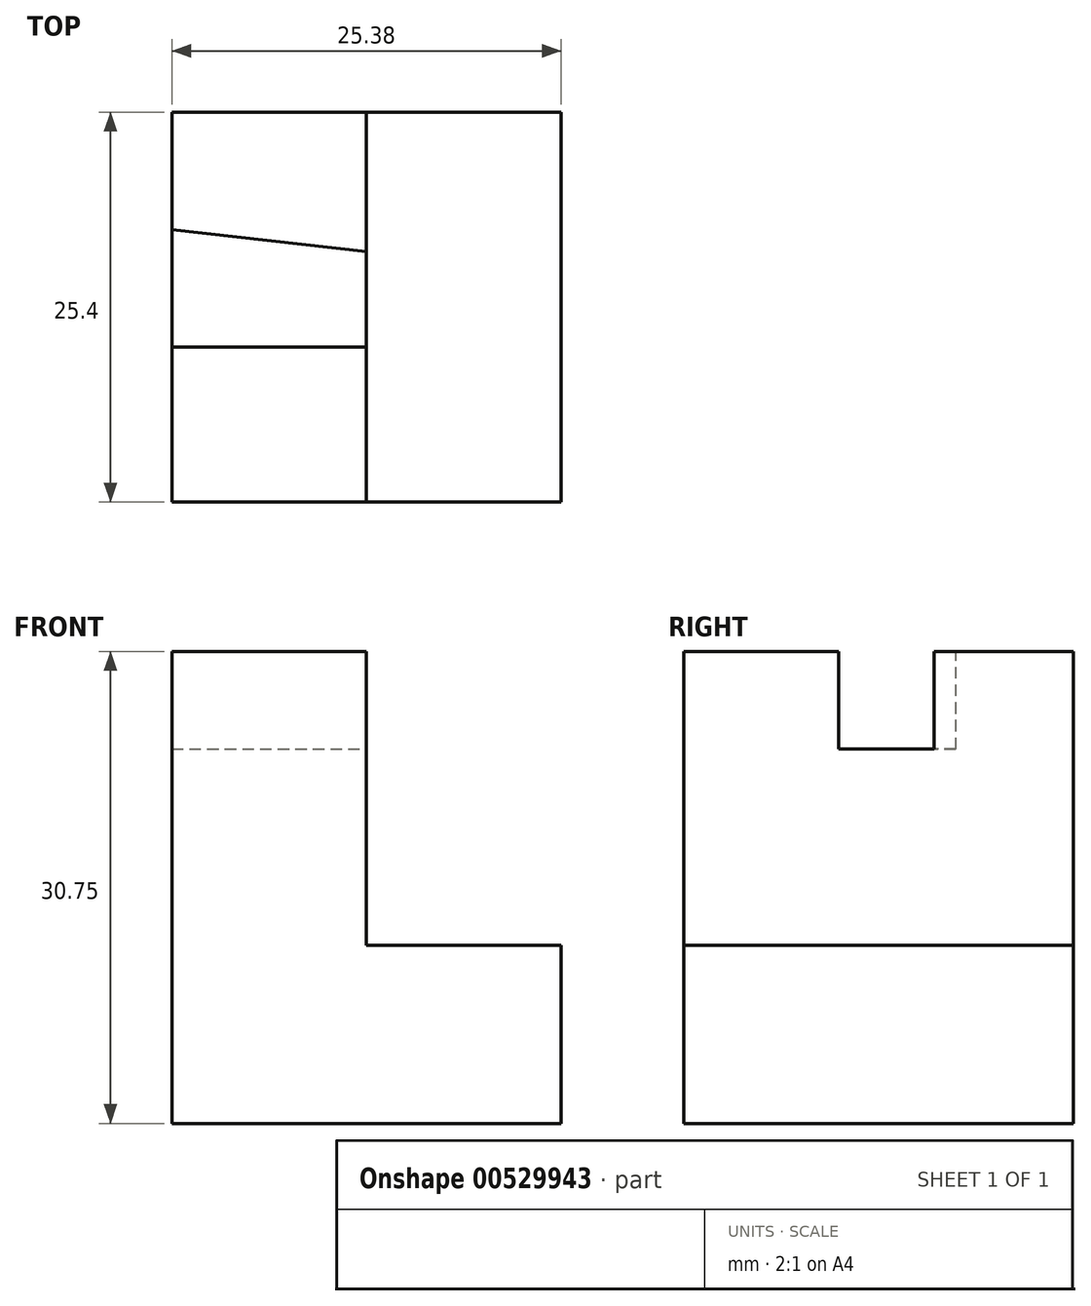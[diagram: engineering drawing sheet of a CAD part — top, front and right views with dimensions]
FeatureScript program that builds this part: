
annotation { "Feature Type Name" : "Feature", "Feature Type Description" : "" }
export const myFeature = defineFeature(function(context is Context, id is Id, definition is map)
    precondition{}
    {
        {
            var Q0;
            Q0=qCreatedBy(makeId("Front.planeOp"),FACE);
            var sketch = newSketch(context, id + "F0", { "sketchPlane" : qUnion([Q0])});
            skLineSegment(sketch, "E0.bottom", {"start": v(-57, 56.92) * mm, "end": v(-18.9, 56.92) * mm});
            skLineSegment(sketch, "E0.top", {"start": v(-57, 26.17) * mm, "end": v(-18.9, 26.17) * mm});
            skLineSegment(sketch, "E0.left", {"start": v(-57, 56.92) * mm, "end": v(-57, 26.17) * mm});
            skLineSegment(sketch, "E0.right", {"start": v(-18.9, 56.92) * mm, "end": v(-18.9, 26.17) * mm});
            skSolve(sketch);
        }
        {
            var Q0;
            Q0=makeQuery(id+"F0.imprint","IMPRINT",FACE,{"disambiguationData":[TD([[makeQuery(id+"F0.imprint","IMPRINT",EDGE,{"derivedFrom":sQuery(id+"F0.wireOp",EDGE,"E0.bottom")}),-1.0]])]});
            extrude(context, id + "F1", {"entities" : qUnion([Q0]), "depth" : 25.4 * mm, "offsetDistance" : 25.4 * mm});
        }
        {
            var Q0;
            Q0=makeQuery(id+"F1.opExtrude","SWEPT_FACE",FACE,{"disambiguationData":[OSD([sQuery(id+"F0.wireOp",EDGE,"E0.right")])]});
            var sketch = newSketch(context, id + "F2", { "sketchPlane" : qUnion([Q0])});
            skLineSegment(sketch, "E1", {"start": v(-25.4, 56.92) * mm, "end": v(-25.4, 37.78) * mm});
            skLineSegment(sketch, "E2", {"start": v(-25.4, 37.78) * mm, "end": v(0, 37.78) * mm});
            skLineSegment(sketch, "E3", {"start": v(0, 37.78) * mm, "end": v(0, 56.92) * mm});
            skLineSegment(sketch, "E4", {"start": v(0, 56.92) * mm, "end": v(-25.4, 56.92) * mm});
            skSolve(sketch);
        }
        {
            var Q0;
            Q0=makeQuery(id+"F2.imprint","IMPRINT",FACE,{"disambiguationData":[TD([[makeQuery(id+"F2.imprint","IMPRINT",EDGE,{"derivedFrom":sQuery(id+"F2.wireOp",EDGE,"E1")}),1.0]])]});
            extrude(context, id + "F3", {"entities" : qUnion([Q0]), "operationType" : NewBodyOperationType.REMOVE, "oppositeDirection" : true, "depth" : 12.7 * mm, "offsetDistance" : 25.4 * mm});
        }
        {
            var Q0;
            Q0=makeQuery(id+"F1.opExtrude","CAP_FACE",FACE,{"disambiguationData":[OSD([sQuery(id+"F0.wireOp",EDGE,"E0.bottom"),sQuery(id+"F0.wireOp",EDGE,"E0.top"),sQuery(id+"F0.wireOp",EDGE,"E0.left"),sQuery(id+"F0.wireOp",EDGE,"E0.right")])],"isStart":true});
            var sketch = newSketch(context, id + "F4", { "sketchPlane" : qUnion([Q0])});
            skLineSegment(sketch, "E5", {"start": v(18.9, 26.17) * mm, "end": v(44.28, 26.17) * mm});
            skLineSegment(sketch, "E6", {"start": v(44.28, 26.17) * mm, "end": v(44.28, 56.92) * mm});
            skSolve(sketch);
        }
        {
            var Q0;
            {var subQ0=sQuery(id+"F4.wireOp",EDGE,"E6");Q0=makeQuery(id+"F4.imprint","IMPRINT",FACE,{"disambiguationData":[TD([[makeQuery(id+"F4.imprint","IMPRINT",EDGE,{"derivedFrom":subQ0}),-1.0]])]});}
            extrude(context, id + "F5", {"entities" : qUnion([Q0]), "operationType" : NewBodyOperationType.REMOVE, "oppositeDirection" : true, "depth" : 25.4 * mm, "offsetDistance" : 25.4 * mm});
        }
        {
            var Q0;
            Q0=makeQuery(id+"F1.opExtrude","SWEPT_FACE",FACE,{"disambiguationData":[OSD([sQuery(id+"F0.wireOp",EDGE,"E0.bottom")])]});
            var sketch = newSketch(context, id + "F6", { "sketchPlane" : qUnion([Q0])});
            skLineSegment(sketch, "E7", {"start": v(-44.28, -25.4) * mm, "end": v(-44.28, -15.31) * mm});
            skLineSegment(sketch, "E8", {"start": v(-44.28, -15.31) * mm, "end": v(-31.6, -15.31) * mm});
            skLineSegment(sketch, "E9", {"start": v(-31.6, -15.31) * mm, "end": v(-31.6, -25.4) * mm});
            skLineSegment(sketch, "E10", {"start": v(-31.6, -25.4) * mm, "end": v(-44.28, -25.4) * mm});
            skLineSegment(sketch, "E11", {"start": v(-44.28, 0) * mm, "end": v(-44.28, -7.65) * mm});
            skLineSegment(sketch, "E12", {"start": v(-44.28, -7.65) * mm, "end": v(-31.6, -9.1) * mm});
            skLineSegment(sketch, "E13", {"start": v(-31.6, -9.1) * mm, "end": v(-31.6, 0) * mm});
            skLineSegment(sketch, "E14", {"start": v(-31.6, 0) * mm, "end": v(-44.28, 0) * mm});
            skSolve(sketch);
        }
        {
            var Q0;
            {var subQ0=sQuery(id+"F6.wireOp",EDGE,"E8");Q0=makeQuery(id+"F6.imprint","IMPRINT",FACE,{"disambiguationData":[TD([[makeQuery(id+"F6.imprint","IMPRINT",EDGE,{"derivedFrom":subQ0}),1.0]])]});}
            extrude(context, id + "F7", {"entities" : qUnion([Q0]), "operationType" : NewBodyOperationType.REMOVE, "oppositeDirection" : true, "depth" : 6.35 * mm, "offsetDistance" : 25.4 * mm});
        }
    });
